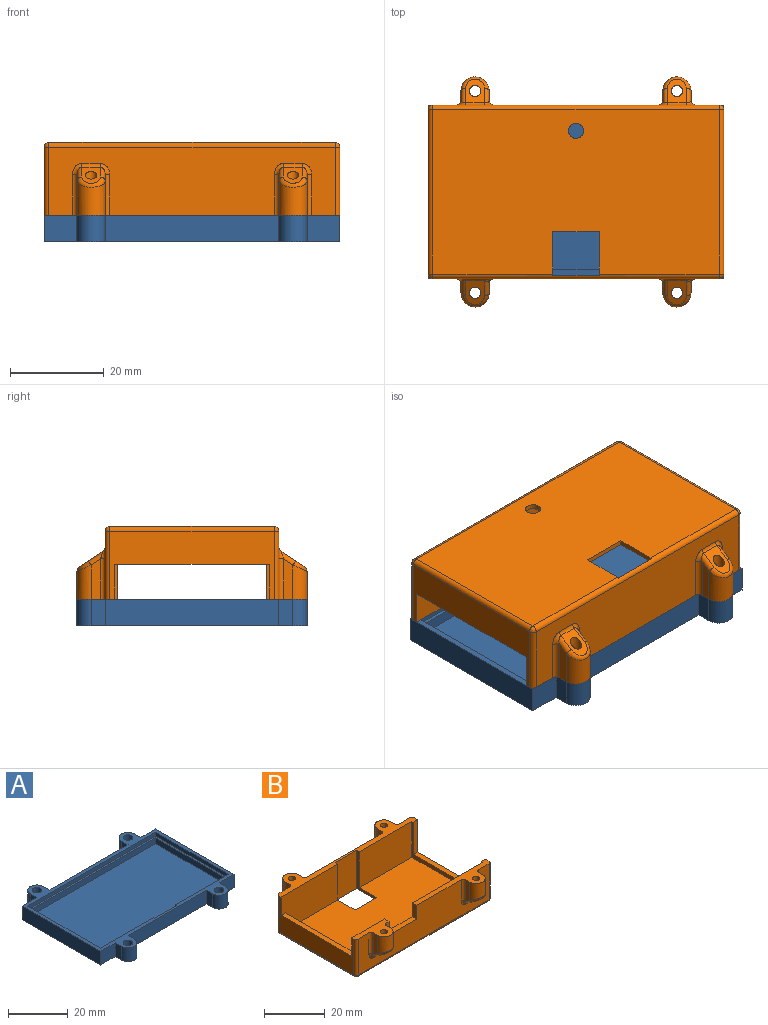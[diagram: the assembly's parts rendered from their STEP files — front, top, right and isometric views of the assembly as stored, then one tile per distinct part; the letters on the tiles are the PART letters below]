
ASSEMBLY  parts=2 mates=1
PART A: 41 faces, bbox 63x49x5.6 mm
  f0: plane 60.4x34.4mm, normal (0,0,1), area 123.5mm2, adj f1,f2,f4,f5,f6,f8,f9,f10
  f1: plane 59x2.4mm, normal (0,1,0), area 131.2mm2, adj f0,f5,f6,f7,f37,f39,f40
  f2: plane 25x1.6mm, normal (0,1,0), area 40mm2, adj f0,f3,f10,f37
  f3: plane 63x49mm, normal (0,0,1), area 343.4mm2, adj f2,f8,f9,f10,f11,f12,f13,f14
  f4: plane 59x2.4mm, normal (0,-1,0), area 141.6mm2, adj f0,f5,f6,f7
  f5: plane 33x2.4mm, normal (-1,0,0), area 79.2mm2, adj f0,f1,f4,f7
  f6: plane 33x2.4mm, normal (1,0,0), area 79.2mm2, adj f0,f1,f4,f7
  f7: plane 59x33mm, normal (0,0,1), area 1947mm2, adj f1,f4,f5,f6
  f8: plane 34.4x1.6mm, normal (-1,0,0), area 55mm2, adj f0,f3,f9,f11
  f9: plane 25x1.6mm, normal (0,1,0), area 40mm2, adj f0,f3,f8,f39
  f10: plane 34.4x1.6mm, normal (1,0,0), area 55mm2, adj f0,f2,f3,f11
  f11: plane 60.4x1.6mm, normal (0,-1,0), area 96.6mm2, adj f0,f3,f8,f10
  f12: cylinder r=1.6mm len=5.6mm, axis (0,0,-1), area 56.3mm2, adj f3,f16
  f13: cylinder r=1.6mm len=5.6mm, axis (0,0,-1), area 56.3mm2, adj f3,f16
  f14: cylinder r=1.6mm len=5.6mm, axis (0,0,-1), area 56.3mm2, adj f3,f16
  f15: cylinder r=1.6mm len=5.6mm, axis (0,0,-1), area 56.3mm2, adj f3,f16
  f16: plane 63x49mm, normal (0,0,-1), area 2427.4mm2, adj f12,f13,f14,f15,f17,f18,f19,f20
  f17: plane 5.6x3mm, normal (1,0,0), area 16.8mm2, adj f3,f16,f18,f36
  f18: plane 7x5.6mm, normal (0,1,0), area 39.2mm2, adj f3,f16,f17,f19
  f19: plane 37x5.6mm, normal (1,0,0), area 207.2mm2, adj f3,f16,f18,f20
  f20: plane 7x5.6mm, normal (0,-1,0), area 39.2mm2, adj f3,f16,f19,f21
  f21: plane 5.6x3mm, normal (1,0,0), area 16.8mm2, adj f3,f16,f20,f22
  f22: cylinder r=3mm len=6mm, axis (0,0,-1), area 52.8mm2, adj f3,f16,f21,f23
  f23: plane 5.6x3mm, normal (-1,0,0), area 16.8mm2, adj f3,f16,f22,f24
  f24: plane 37x5.6mm, normal (0,-1,0), area 207.2mm2, adj f3,f16,f23,f25
  f25: plane 5.6x3mm, normal (1,0,0), area 16.8mm2, adj f3,f16,f24,f26
  f26: cylinder r=3mm len=6mm, axis (0,0,-1), area 52.8mm2, adj f3,f16,f25,f27
  f27: plane 5.6x3mm, normal (-1,0,0), area 16.8mm2, adj f3,f16,f26,f28
  f28: plane 7x5.6mm, normal (0,-1,0), area 39.2mm2, adj f3,f16,f27,f29
  f29: plane 37x5.6mm, normal (-1,0,0), area 207.2mm2, adj f3,f16,f28,f30
  f30: plane 7x5.6mm, normal (0,1,0), area 39.2mm2, adj f3,f16,f29,f31
  f31: plane 5.6x3mm, normal (-1,0,0), area 16.8mm2, adj f3,f16,f30,f32
  f32: cylinder r=3mm len=6mm, axis (0,0,-1), area 52.8mm2, adj f3,f16,f31,f33
  f33: plane 5.6x3mm, normal (1,0,0), area 16.8mm2, adj f3,f16,f32,f34
  f34: plane 37x5.6mm, normal (0,1,0), area 207.2mm2, adj f3,f16,f33,f35
  f35: plane 5.6x3mm, normal (-1,0,0), area 16.8mm2, adj f3,f16,f34,f36
  f36: cylinder r=3mm len=6mm, axis (0,0,-1), area 52.8mm2, adj f3,f16,f17,f35
  f37: plane 2.6x1.3mm, normal (1,0,0), area 2.3mm2, adj f0,f1,f2,f3,f38,f40
  f38: plane 10.4x2.6mm, normal (0,1,0), area 27mm2, adj f3,f37,f39,f40
  f39: plane 2.6x1.3mm, normal (-1,0,0), area 2.3mm2, adj f0,f1,f3,f9,f38,f40
  f40: plane 10.4x1.3mm, normal (0,0,1), area 13.5mm2, adj f1,f37,f38,f39
PART B: 90 faces, bbox 63x49x15.5 mm
  f0: plane 61x35mm, normal (0,0,-1), area 2037mm2, adj f2,f27,f75,f76,f80,f86,f87,f88
  f1: plane 24.5x14.5mm, normal (0,-1,0), area 355.2mm2, adj f15,f16,f31,f88
  f2: cylinder r=1mm len=61mm, axis (-1,0,0), area 92.8mm2, adj f0,f29,f79,f81,f87,f88,f89
  f3: plane 34.85x8.61mm, normal (0,0,1), area 98.7mm2, adj f4,f15,f21,f22,f23,f24,f25,f28
  f4: plane 61x14.5mm, normal (0,1,0), area 799.9mm2, adj f3,f13,f14,f15,f16,f17,f35,f83
  f5: plane 8.63x2mm, normal (1,0,0), area 15.9mm2, adj f6,f31,f40,f41
  f6: cylinder r=3mm len=7.3mm, axis (0,0,-1), area 60.8mm2, adj f5,f7,f31,f43
  f7: plane 8.63x2mm, normal (-1,0,0), area 15.9mm2, adj f6,f31,f45,f47
  f8: plane 8.63x2mm, normal (1,0,0), area 15.9mm2, adj f9,f31,f57,f58
  f9: cylinder r=3mm len=7.3mm, axis (0,0,-1), area 60.8mm2, adj f8,f10,f31,f56
  f10: plane 8.63x2mm, normal (-1,0,0), area 15.9mm2, adj f9,f31,f59,f60
  f11: cylinder r=1.2mm len=9.3mm, axis (0,0,-1), area 64.1mm2, adj f31,f39
  f12: cylinder r=1.2mm len=9.3mm, axis (0,0,-1), area 64.1mm2, adj f31,f37
  f13: plane 33x7.1mm, normal (1,0,0), area 234.3mm2, adj f4,f16,f30,f35
  f14: plane 15.35x8mm, normal (0,0,1), area 58.5mm2, adj f4,f17,f18,f19,f20,f24,f26,f66
  f15: plane 33x14.5mm, normal (-1,0,0), area 65.3mm2, adj f1,f3,f4,f16,f31,f32,f33,f34
  f16: plane 59x33mm, normal (0,0,1), area 1859mm2, adj f1,f4,f13,f15,f27,f30,f86,f87
  f17: plane 35x14.5mm, normal (-1,0,0), area 263.3mm2, adj f4,f14,f30,f31,f35,f74,f80,f82
  f18: plane 8.63x2mm, normal (-1,0,0), area 15.9mm2, adj f14,f19,f67,f68
  f19: cylinder r=3mm len=7.3mm, axis (0,0,-1), area 60.8mm2, adj f14,f18,f20,f64
  f20: plane 8.63x2mm, normal (1,0,0), area 15.9mm2, adj f14,f19,f65,f66
  f21: plane 8.63x2mm, normal (-1,0,0), area 15.9mm2, adj f3,f22,f48,f49
  f22: cylinder r=3mm len=7.3mm, axis (0,0,-1), area 60.8mm2, adj f3,f21,f23,f51
  f23: plane 8.63x2mm, normal (1,0,0), area 15.9mm2, adj f3,f22,f53,f55
  f24: plane 61x14.5mm, normal (0,-1,0), area 641.7mm2, adj f3,f14,f48,f50,f52,f54,f55,f66
  f25: plane 35x14.5mm, normal (1,0,0), area 94.3mm2, adj f3,f31,f32,f33,f34,f72,f76,f77
  f26: cylinder r=1.2mm len=9.3mm, axis (0,0,-1), area 64.1mm2, adj f14,f38
  f27: cylinder r=1.6mm len=3.2mm, axis (0,0,-1), area 10.1mm2, adj f0,f16
  f28: cylinder r=1.2mm len=9.3mm, axis (0,0,-1), area 64.1mm2, adj f3,f36
  f29: plane 61x14.5mm, normal (0,1,0), area 712.1mm2, adj f2,f31,f40,f42,f44,f46,f47,f57
  f30: plane 26.5x14.5mm, normal (0,-1,0), area 370mm2, adj f13,f16,f17,f31,f35,f87
  f31: plane 63x8.61mm, normal (0,0,1), area 169.9mm2, adj f1,f5,f6,f7,f8,f9,f10,f11
  f32: plane 13x2mm, normal (0,-1,0), area 26mm2, adj f15,f25,f31,f34
  f33: plane 13x2mm, normal (0,1,0), area 26mm2, adj f3,f15,f25,f34
  f34: plane 31.79x2mm, normal (0,0,1), area 63.6mm2, adj f15,f25,f32,f33
  f35: plane 33x2mm, normal (0,0,1), area 66mm2, adj f4,f13,f17,f30
  f36: plane 5.11x4mm, normal (0,-0.55,-0.83), area 17.1mm2, adj f28,f49,f51,f52,f53
  f37: plane 5.11x4mm, normal (0,0.55,-0.83), area 17.1mm2, adj f12,f41,f43,f44,f45
  f38: plane 5.11x4mm, normal (0,-0.55,-0.83), area 17.1mm2, adj f26,f64,f65,f68,f71
  f39: plane 5.11x4mm, normal (0,0.55,-0.83), area 17.1mm2, adj f11,f56,f58,f59,f63
  f40: cylinder r=1mm len=8.63mm, axis (0,0,-1), area 13.6mm2, adj f5,f29,f31,f42
  f41: cylinder r=1mm len=3.66mm, axis (0,0.83,0.55), area 5.1mm2, adj f5,f37,f42,f43
  f42: bspline ~2.82x2.35mm, area 3.2mm2, adj f29,f40,f41,f44
  f43: bspline ~6.12x3.52mm, area 10.4mm2, adj f6,f37,f41,f45
  f44: cylinder r=1mm len=4mm, axis (-1,0,0), area 3.9mm2, adj f29,f37,f42,f46
  f45: cylinder r=1mm len=3.66mm, axis (0,-0.83,-0.55), area 5.1mm2, adj f7,f37,f43,f46
  f46: bspline ~2.82x2mm, area 3.2mm2, adj f29,f44,f45,f47
  f47: cylinder r=1mm len=8.63mm, axis (0,0,1), area 13.6mm2, adj f7,f29,f31,f46
  f48: cylinder r=1mm len=8.63mm, axis (0,0,-1), area 13.6mm2, adj f3,f21,f24,f50
  f49: cylinder r=1mm len=3.66mm, axis (0,-0.83,0.55), area 5.1mm2, adj f21,f36,f50,f51
  f50: bspline ~2.82x2.35mm, area 3.2mm2, adj f24,f48,f49,f52
  f51: bspline ~6.12x3.52mm, area 10.4mm2, adj f22,f36,f49,f53
  f52: cylinder r=1mm len=4mm, axis (1,0,0), area 3.9mm2, adj f24,f36,f50,f54
  f53: cylinder r=1mm len=3.66mm, axis (0,0.83,-0.55), area 5.1mm2, adj f23,f36,f51,f54
  f54: bspline ~2.82x2mm, area 3.2mm2, adj f24,f52,f53,f55
  f55: cylinder r=1mm len=8.63mm, axis (0,0,1), area 13.6mm2, adj f3,f23,f24,f54
  f56: bspline ~6.12x3.52mm, area 10.4mm2, adj f9,f39,f58,f59
  f57: cylinder r=1mm len=8.63mm, axis (0,0,-1), area 13.6mm2, adj f8,f29,f31,f61
  f58: cylinder r=1mm len=3.66mm, axis (0,0.83,0.55), area 5.1mm2, adj f8,f39,f56,f61
  f59: cylinder r=1mm len=3.66mm, axis (0,-0.83,-0.55), area 5.1mm2, adj f10,f39,f56,f62
  f60: cylinder r=1mm len=8.63mm, axis (0,0,1), area 13.6mm2, adj f10,f29,f31,f62
  f61: bspline ~2.82x2.35mm, area 3.2mm2, adj f29,f57,f58,f63
  f62: bspline ~2.82x2mm, area 3.2mm2, adj f29,f59,f60,f63
  f63: cylinder r=1mm len=4mm, axis (-1,0,0), area 3.9mm2, adj f29,f39,f61,f62
  f64: bspline ~6.12x3.52mm, area 10.4mm2, adj f19,f38,f65,f68
  f65: cylinder r=1mm len=3.66mm, axis (0,0.83,-0.55), area 5.1mm2, adj f20,f38,f64,f69
  f66: cylinder r=1mm len=8.63mm, axis (0,0,1), area 13.6mm2, adj f14,f20,f24,f69
  f67: cylinder r=1mm len=8.63mm, axis (0,0,-1), area 13.6mm2, adj f14,f18,f24,f70
  f68: cylinder r=1mm len=3.66mm, axis (0,-0.83,0.55), area 5.1mm2, adj f18,f38,f64,f70
  f69: bspline ~2.82x2mm, area 3.2mm2, adj f24,f65,f66,f71
  f70: bspline ~2.82x2.35mm, area 3.2mm2, adj f24,f67,f68,f71
  f71: cylinder r=1mm len=4mm, axis (1,0,0), area 3.9mm2, adj f24,f38,f69,f70
  f72: cylinder r=1mm len=14.5mm, axis (0,0,-1), area 22.8mm2, adj f3,f24,f25,f73
  f73: sphere r=1mm, area 1.6mm2, adj f72,f75,f76
  f74: cylinder r=1mm len=14.5mm, axis (0,0,-1), area 22.8mm2, adj f14,f17,f24,f78
  f75: cylinder r=1mm len=61mm, axis (1,0,0), area 95.8mm2, adj f0,f24,f73,f78
  f76: cylinder r=1mm len=35mm, axis (0,1,0), area 55mm2, adj f0,f25,f73,f79
  f77: cylinder r=1mm len=14.5mm, axis (0,0,-1), area 22.8mm2, adj f25,f29,f31,f79
  f78: sphere r=1mm, area 1.6mm2, adj f74,f75,f80
  f79: sphere r=1mm, area 1.6mm2, adj f2,f76,f77
  f80: cylinder r=1mm len=35mm, axis (0,-1,0), area 55mm2, adj f0,f17,f78,f81
  f81: sphere r=1mm, area 1.6mm2, adj f2,f80,f82
  f82: cylinder r=1mm len=14.5mm, axis (0,0,-1), area 22.8mm2, adj f17,f29,f31,f81
  f83: plane 5.5x2mm, normal (1,0,0), area 11mm2, adj f4,f14,f24,f85
  f84: plane 5.5x2mm, normal (-1,0,0), area 11mm2, adj f3,f4,f24,f85
  f85: plane 12.8x2mm, normal (0,0,1), area 25.6mm2, adj f4,f24,f83,f84
  f86: plane 10x1mm, normal (0,1,0), area 10mm2, adj f0,f16,f87,f88
  f87: plane 15.5x9.3mm, normal (1,0,0), area 28.1mm2, adj f0,f2,f16,f30,f31,f86,f89
  f88: plane 15.5x9.3mm, normal (-1,0,0), area 28.1mm2, adj f0,f1,f2,f16,f31,f86,f89
  f89: plane 15.45x10mm, normal (0,-1,0), area 154.5mm2, adj f2,f31,f87,f88
PLACE A t=(-36.91,11.27,-5.37)mm
PLACE B rot(axis=(1,0,0),180deg) t=(-36.91,-15.73,15.73)mm
MATE fastened B.f19 <-> A.f12  axis (0,0,1) through (-53.87,19.27,0.23)mm
